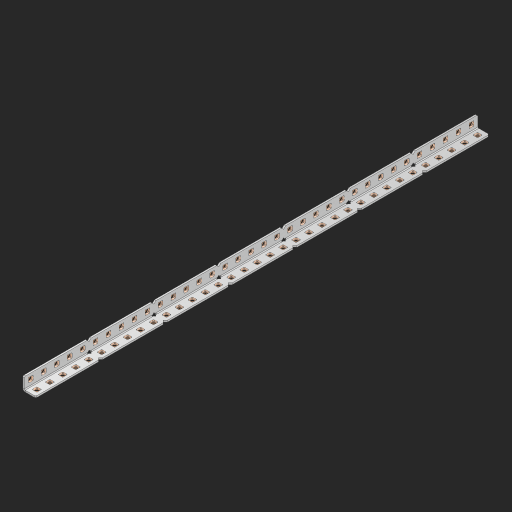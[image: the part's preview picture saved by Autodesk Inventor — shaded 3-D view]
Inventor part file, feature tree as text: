
AUTODESK INVENTOR PART (.ipt)
format: ipt  version: 2023 (Build 270158000, 158)  size: 1,057,280 bytes
history: native  units: in
note: dims shown in document units (in); Inventor stores cm internally (conversion verified against a paired STEP export)
features: other x112, extrude x71, sheet_metal_op x8, sketch x5, pattern_linear x1, mirror x1, chamfer x1
ambient origin geometry x8: Origin, YZ Plane, XZ Plane, XY Plane, X Axis, Y Axis, Z Axis, Center Point
bodies: Solid1 (feature_tree), Body (feature_tree)
feature tree (199):
  other  "Table"
  other  "Alu Angle 1x1x35"
  other  "Alu Angle 1x1x34"
  other  "Alu Angle 1x1x33"
  other  "Alu Angle 1x1x32"
  other  "Alu Angle 1x1x31"
  other  "Alu Angle 1x1x30"
  other  "Alu Angle 1x1x29"
  other  "Alu Angle 1x1x28"
  other  "Alu Angle 1x1x27"
  other  "Alu Angle 1x1x26"
  other  "Alu Angle 1x1x25"
  other  "Alu Angle 1x1x24"
  other  "Alu Angle 1x1x23"
  other  "Alu Angle 1x1x22"
  other  "Alu Angle 1x1x21"
  other  "Alu Angle 1x1x20"
  other  "Alu Angle 1x1x19"
  other  "Alu Angle 1x1x18"
  other  "Alu Angle 1x1x17"
  other  "Alu Angle 1x1x16"
  other  "Alu Angle 1x1x15"
  other  "Alu Angle 1x1x14"
  other  "Alu Angle 1x1x13"
  other  "Alu Angle 1x1x12"
  other  "Alu Angle 1x1x11"
  other  "Alu Angle 1x1x10"
  other  "Alu Angle 1x1x9"
  other  "Alu Angle 1x1x8"
  other  "Alu Angle 1x1x7"
  other  "Alu Angle 1x1x6"
  other  "Alu Angle 1x1x5"
  other  "Alu Angle 1x1x4"
  other  "Alu Angle 1x1x3"
  other  "Alu Angle 1x1x2"
  other  "Alu Angle 1x1x1"
  sheet_metal_op  "Flanges"
  sheet_metal_op  "Body Pattern"
  other  "Arc Length"
  pattern_linear  "Notch Pattern"  Spacing1=0.125in  [1 undecoded]
  other  "Diagonal Plane"
  mirror  "Everything Mirrored"
  chamfer  "End Chamfer"
  sketch  "Sketch1"  dims[d0=0.5in]
  other  "Plate1"
  sketch  "Sketch2"  dims[d1=17.5in]
  other  "Plate2"
  sheet_metal_op  "Bend1"
  sheet_metal_op  "Corner1"
  sketch  "Sketch8"  dims[d2=0.0625in]
  sketch  "Sketch9"  dims[d3=0.0625in]
  other  "Srf91"
  sheet_metal_op  "Body Pattern Sketch"
  other  "Srf92"
  sketch  "Sketch13"  dims[d4=0.0312in d5=0.125in d6=0.0625in d7=0.5in d8=90.0deg d9=0.0312in d10=0.25in d11=0.0625in d12=0.0625in d49=0.182in d50=0.02in d52=0.25in d53=0.0625in d54=0.0in d55=0.172in d56=1.0in d57=0.0in d85=0.1473in d86=0.1782in d89=0.0625in d90=0.0in d91=0.04in d92=0.0491in d95=2.5in d96=0.04in d97=0.25in d98=45.0deg d123=0.204in d126=0.0491in d127=0.1473in d128=0.08in d129=0.04in d130=2.5in d131=13.7795in d133=0.5in d134=0.3937in d136=1.0in]
  other  "Srf856"
  other  "Srf857"
  other  "Srf858"
  other  "Srf859"
  other  "Srf860"
  other  "Srf861"
  other  "Srf1275"
  other  "Srf1276"
  other  "Srf1278"
  other  "Srf1279"
  other  "Srf1280"
  other  "Srf1281"
  other  "Srf1282"
  other  "Srf1283"
  other  "Srf1383"
  other  "Srf1384"
  other  "Srf1385"
  other  "Srf1386"
  other  "Srf1387"
  other  "Srf1388"
  other  "Srf1389"
  other  "Srf1390"
  other  "Srf1391"
  other  "Srf1392"
  other  "Srf1393"
  other  "Srf1394"
  other  "Srf1395"
  other  "Srf1396"
  other  "Srf1397"
  other  "Srf1398"
  other  "Srf1399"
  other  "Srf1400"
  other  "Srf1401"
  other  "Srf1402"
  other  "Srf1403"
  other  "Srf1404"
  other  "Srf1405"
  other  "Srf1406"
  other  "Srf1407"
  other  "Srf1408"
  other  "Srf1409"
  other  "Srf1475"
  other  "Srf1476"
  other  "Srf1477"
  other  "Srf1478"
  other  "Srf1479"
  other  "Srf1480"
  other  "Srf1481"
  other  "Srf1482"
  other  "Srf1483"
  other  "Srf1484"
  other  "Srf1485"
  other  "Srf1486"
  other  "Srf1487"
  other  "Srf1488"
  other  "Srf1489"
  other  "Srf1490"
  other  "Srf1491"
  other  "Srf1492"
  other  "Srf1493"
  other  "Srf1494"
  other  "Srf1495"
  other  "Srf1496"
  other  "Srf1497"
  other  "Srf1498"
  other  "Srf1499"
  other  "Srf1500"
  other  "Srf1501"
  other  "Srf1568"
  other  "Srf1569"
  sheet_metal_op  "Body Stamp"
  sheet_metal_op  "Body Circle"
  sheet_metal_op  "Notch"
  extrude  "ExtrusionSrf92"  Depth=0.0625in
  extrude  "ExtrusionSrf856"  Depth=0.5in TaperAngle=90.0deg
  extrude  "ExtrusionSrf857"  Depth=0.25in
  extrude  "ExtrusionSrf858"  Depth=0.0625in
  extrude  "ExtrusionSrf859"  Depth=0.0625in
  extrude  "ExtrusionSrf860"  Depth=0.3937in
  extrude  "ExtrusionSrf861"  Depth=0.02in
  extrude  "ExtrusionSrf1275"  Depth=0.25in
  extrude  "ExtrusionSrf1276"  Depth=0.0625in
  extrude  "ExtrusionSrf1277"  TaperAngle=0.0deg  [1 undecoded]
  extrude  "ExtrusionSrf1278"  Depth=0.3937in
  extrude  "ExtrusionSrf1279"  Depth=0.3937in TaperAngle=0.0deg
  extrude  "ExtrusionSrf1280"  Depth=0.3937in
  extrude  "ExtrusionSrf1281"  Depth=0.3937in
  extrude  "ExtrusionSrf1282"  Depth=0.0625in
  extrude  "ExtrusionSrf1383"  Depth=0.3937in TaperAngle=0.0deg
  extrude  "ExtrusionSrf1384"  Depth=0.3937in
  extrude  "ExtrusionSrf1385"  Depth=0.25in TaperAngle=45.0deg
  extrude  "ExtrusionSrf1386"  Depth=0.3937in
  extrude  "ExtrusionSrf1387"  Depth=0.3937in
  extrude  "ExtrusionSrf1388"  Depth=0.3937in
  extrude  "ExtrusionSrf1389"  Depth=0.3937in
  extrude  "ExtrusionSrf1390"  Depth=0.3937in
  extrude  "ExtrusionSrf1391"  Depth=0.3937in
  extrude  "ExtrusionSrf1392"  Depth=0.3937in
  extrude  "ExtrusionSrf1393"  Depth=0.5in
  extrude  "ExtrusionSrf1394"  [1 undecoded]
  extrude  "ExtrusionSrf1395"  [1 undecoded]
  extrude  "ExtrusionSrf1396"  [1 undecoded]
  extrude  "ExtrusionSrf1397"  [1 undecoded]
  extrude  "ExtrusionSrf1398"  [1 undecoded]
  extrude  "ExtrusionSrf1399"  [1 undecoded]
  extrude  "ExtrusionSrf1400"  [1 undecoded]
  extrude  "ExtrusionSrf1401"  [1 undecoded]
  extrude  "ExtrusionSrf1402"  [1 undecoded]
  extrude  "ExtrusionSrf1403"  [1 undecoded]
  extrude  "ExtrusionSrf1404"  [1 undecoded]
  extrude  "ExtrusionSrf1405"  [1 undecoded]
  extrude  "ExtrusionSrf1406"  [1 undecoded]
  extrude  "ExtrusionSrf1407"  [1 undecoded]
  extrude  "ExtrusionSrf1408"  [1 undecoded]
  extrude  "ExtrusionSrf1409"  [1 undecoded]
  extrude  "ExtrusionSrf1475"  [1 undecoded]
  extrude  "ExtrusionSrf1476"  [1 undecoded]
  extrude  "ExtrusionSrf1477"  [1 undecoded]
  extrude  "ExtrusionSrf1478"  [1 undecoded]
  extrude  "ExtrusionSrf1479"  [1 undecoded]
  extrude  "ExtrusionSrf1480"  [1 undecoded]
  extrude  "ExtrusionSrf1481"  [1 undecoded]
  extrude  "ExtrusionSrf1482"  [1 undecoded]
  extrude  "ExtrusionSrf1483"  [1 undecoded]
  extrude  "ExtrusionSrf1484"  [1 undecoded]
  extrude  "ExtrusionSrf1485"  [1 undecoded]
  extrude  "ExtrusionSrf1486"  [1 undecoded]
  extrude  "ExtrusionSrf1487"  [1 undecoded]
  extrude  "ExtrusionSrf1488"  [1 undecoded]
  extrude  "ExtrusionSrf1489"  [1 undecoded]
  extrude  "ExtrusionSrf1490"  [1 undecoded]
  extrude  "ExtrusionSrf1491"  [1 undecoded]
  extrude  "ExtrusionSrf1492"  [1 undecoded]
  extrude  "ExtrusionSrf1493"  [1 undecoded]
  extrude  "ExtrusionSrf1494"  [1 undecoded]
  extrude  "ExtrusionSrf1495"  [1 undecoded]
  extrude  "ExtrusionSrf1496"  [1 undecoded]
  extrude  "ExtrusionSrf1497"  [1 undecoded]
  extrude  "ExtrusionSrf1498"  [1 undecoded]
  extrude  "ExtrusionSrf1499"  [1 undecoded]
  extrude  "ExtrusionSrf1500"  [1 undecoded]
  extrude  "ExtrusionSrf1501"  [1 undecoded]
  extrude  "ExtrusionSrf1568"  [1 undecoded]
  extrude  "ExtrusionSrf1569"  [1 undecoded]
note: 47 required parameter values undecoded (feature->parameter linkage not recoverable at this tier; creation-order binding heuristic only, values carry confidence <= 0.55)
